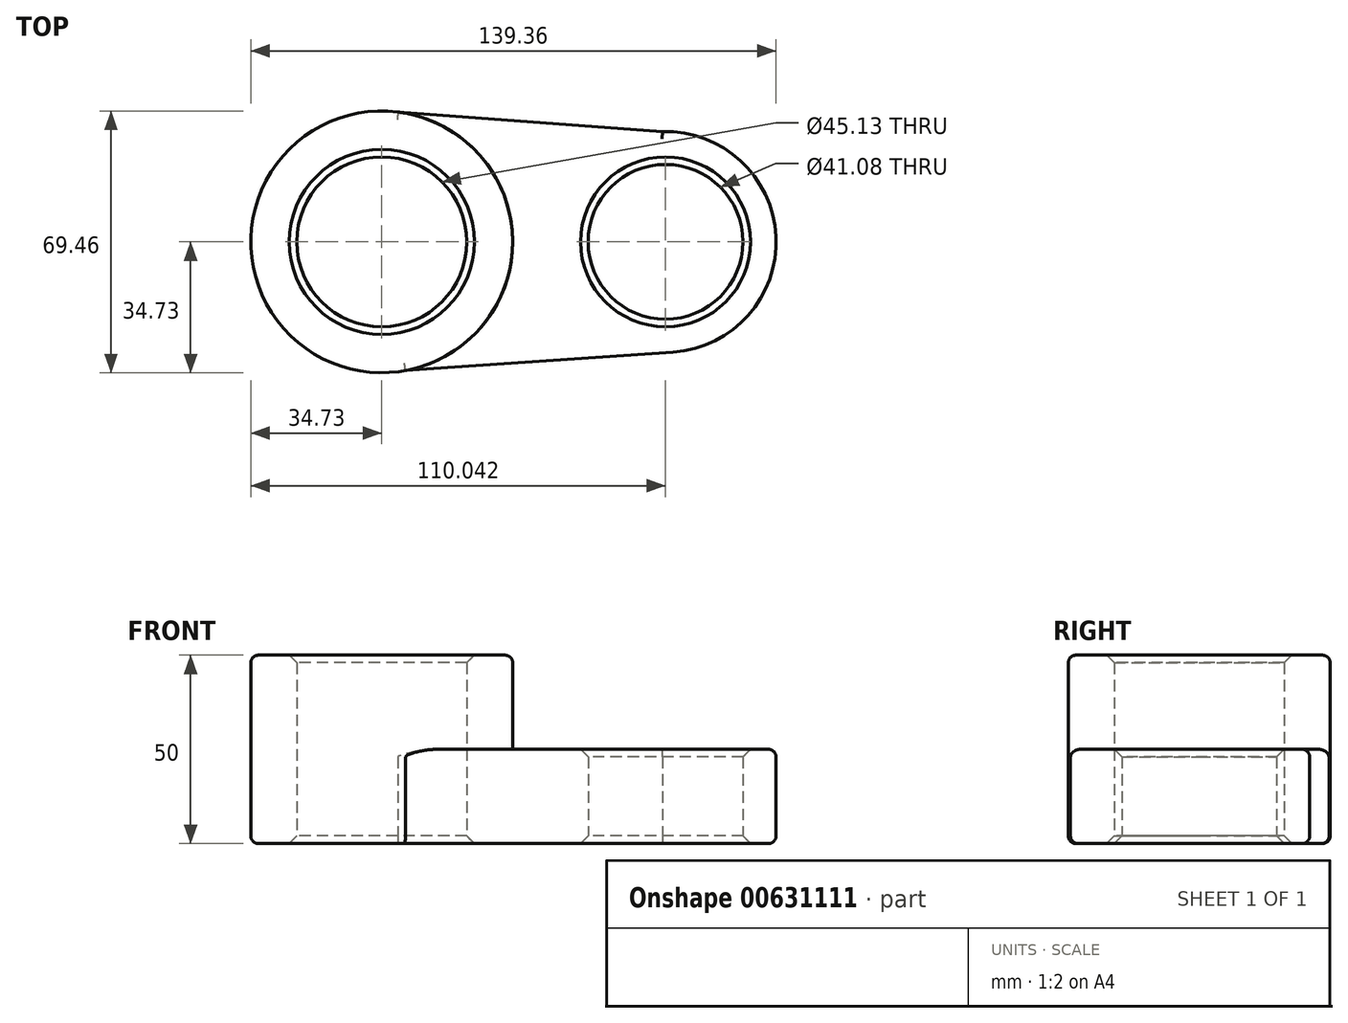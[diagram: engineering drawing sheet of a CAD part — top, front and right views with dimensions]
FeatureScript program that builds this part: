
annotation { "Feature Type Name" : "Feature", "Feature Type Description" : "" }
export const myFeature = defineFeature(function(context is Context, id is Id, definition is map)
    precondition{}
    {
        {
            var Q0;
            Q0=qCreatedBy(makeId("Top.planeOp"),FACE);
            var sketch = newSketch(context, id + "F0", { "sketchPlane" : qUnion([Q0])});
            skCircle(sketch, "E0", {"center": v(0, 0) * mm, "radius": 34.73 * mm});
            skCircle(sketch, "E1", {"center": v(75.31, 0) * mm, "radius": 29.32 * mm});
            skLineSegment(sketch, "E2", {"start": v(4.3, 34.47) * mm, "end": v(74.46, 29.3) * mm});
            skLineSegment(sketch, "E3", {"start": v(6.29, -34.16) * mm, "end": v(77.33, -29.25) * mm});
            skCircle(sketch, "E4", {"center": v(0, 0) * mm, "radius": 22.57 * mm});
            skCircle(sketch, "E5", {"center": v(75.31, 0) * mm, "radius": 20.54 * mm});
            skSolve(sketch);
        }
        {
            var Q0;
            Q0 = qSketchRegion(id + "F0", true);
            extrude(context, id + "F1", {"entities" : qUnion([Q0]), "depth" : 25 * mm, "offsetDistance" : 25 * mm});
        }
        {
            var Q0;
            Q0=makeQuery(id+"F0.imprint","IMPRINT",FACE,{"disambiguationData":[TD([[makeQuery(id+"F0.imprint","IMPRINT",EDGE,{"derivedFrom":sQuery(id+"F0.wireOp",EDGE,"E4")}),-1.0]])]});
            extrude(context, id + "F2", {"entities" : qUnion([Q0]), "operationType" : NewBodyOperationType.ADD, "depth" : 50 * mm, "offsetDistance" : 25 * mm});
        }
        {
            var Q0;
            Q0=makeQuery(id+"F1.opExtrude","CAP_EDGE",EDGE,{"disambiguationData":[OSD([sQuery(id+"F0.wireOp",EDGE,"E1")])],"isStart":false});
            var Q1;
            Q1=makeQuery(id+"F1.opExtrude","CAP_EDGE",EDGE,{"disambiguationData":[OSD([sQuery(id+"F0.wireOp",EDGE,"E3")])],"isStart":false});
            var Q2;
            Q2=makeQuery(id+"F1.opExtrude","CAP_EDGE",EDGE,{"disambiguationData":[OSD([sQuery(id+"F0.wireOp",EDGE,"E2")])],"isStart":false});
            fillet(context, id + "F3", {"entities" : qUnion([Q0, Q1, Q2]), "radius" : 2 * mm, "tangentPropagation" : true, "allowEdgeOverflow" : false});
        }
        {
            var Q0;
            Q0=makeQuery(id+"F1.opExtrude","CAP_EDGE",EDGE,{"disambiguationData":[OSD([sQuery(id+"F0.wireOp",EDGE,"E5")])],"isStart":false});
            var Q1;
            Q1=makeQuery(id+"F2.opExtrude","CAP_EDGE",EDGE,{"disambiguationData":[OSD([sQuery(id+"F0.wireOp",EDGE,"E4")])],"isStart":false});
            chamfer(context, id + "F4", {"entities" : qUnion([Q0, Q1]), "width" : 2 * mm, "tangentPropagation" : true});
        }
        {
            var Q0;
            Q0=makeQuery(id+"F2.opExtrude","CAP_EDGE",EDGE,{"disambiguationData":[OSD([sQuery(id+"F0.wireOp",EDGE,"E0")])],"isStart":false});
            fillet(context, id + "F5", {"entities" : qUnion([Q0]), "radius" : 2 * mm, "tangentPropagation" : true, "allowEdgeOverflow" : false});
        }
        {
            var Q0;
            Q0=makeQuery(id+"F1.opExtrude","CAP_EDGE",EDGE,{"disambiguationData":[OSD([sQuery(id+"F0.wireOp",EDGE,"E2")])],"isStart":true});
            var Q1;
            Q1=makeQuery(id+"F1.opExtrude","CAP_EDGE",EDGE,{"disambiguationData":[OSD([sQuery(id+"F0.wireOp",EDGE,"E1")])],"isStart":true});
            var Q2;
            Q2=makeQuery(id+"F1.opExtrude","CAP_EDGE",EDGE,{"disambiguationData":[OSD([sQuery(id+"F0.wireOp",EDGE,"E0")])],"isStart":true});
            fillet(context, id + "F6", {"entities" : qUnion([Q0, Q1, Q2]), "radius" : 2 * mm, "tangentPropagation" : true, "allowEdgeOverflow" : false});
        }
        {
            var Q0;
            Q0=makeQuery(id+"F1.opExtrude","CAP_EDGE",EDGE,{"disambiguationData":[OSD([sQuery(id+"F0.wireOp",EDGE,"E5")])],"isStart":true});
            var Q1;
            Q1=makeQuery(id+"F1.opExtrude","CAP_EDGE",EDGE,{"disambiguationData":[OSD([sQuery(id+"F0.wireOp",EDGE,"E4")])],"isStart":true});
            chamfer(context, id + "F7", {"entities" : qUnion([Q0, Q1]), "width" : 2 * mm, "tangentPropagation" : true});
        }
    });
